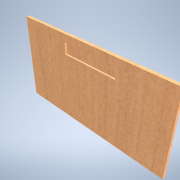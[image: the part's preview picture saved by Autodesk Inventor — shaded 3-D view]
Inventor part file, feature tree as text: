
AUTODESK INVENTOR PART (.ipt)
format: ipt  version: 2021 (Build 250183000, 183)  size: 129,536 bytes
history: native  units: mm
features: sketch x2, extrude x1
ambient origin geometry x8: Origin, YZ Plane, XZ Plane, XY Plane, X Axis, Y Axis, Z Axis, Center Point
bodies: Solid1 (feature_tree)
feature tree (3):
  extrude  "Extrusion1"  Depth=77.0mm
  sketch  "Sketch1"  dims[d0=144.0mm d1=77.0mm]
  sketch  "Sketch4"  dims[d2=3.0mm d3=0.0mm d47=50.0mm d48=10.0mm d49=1.5mm d50=0.0mm]
